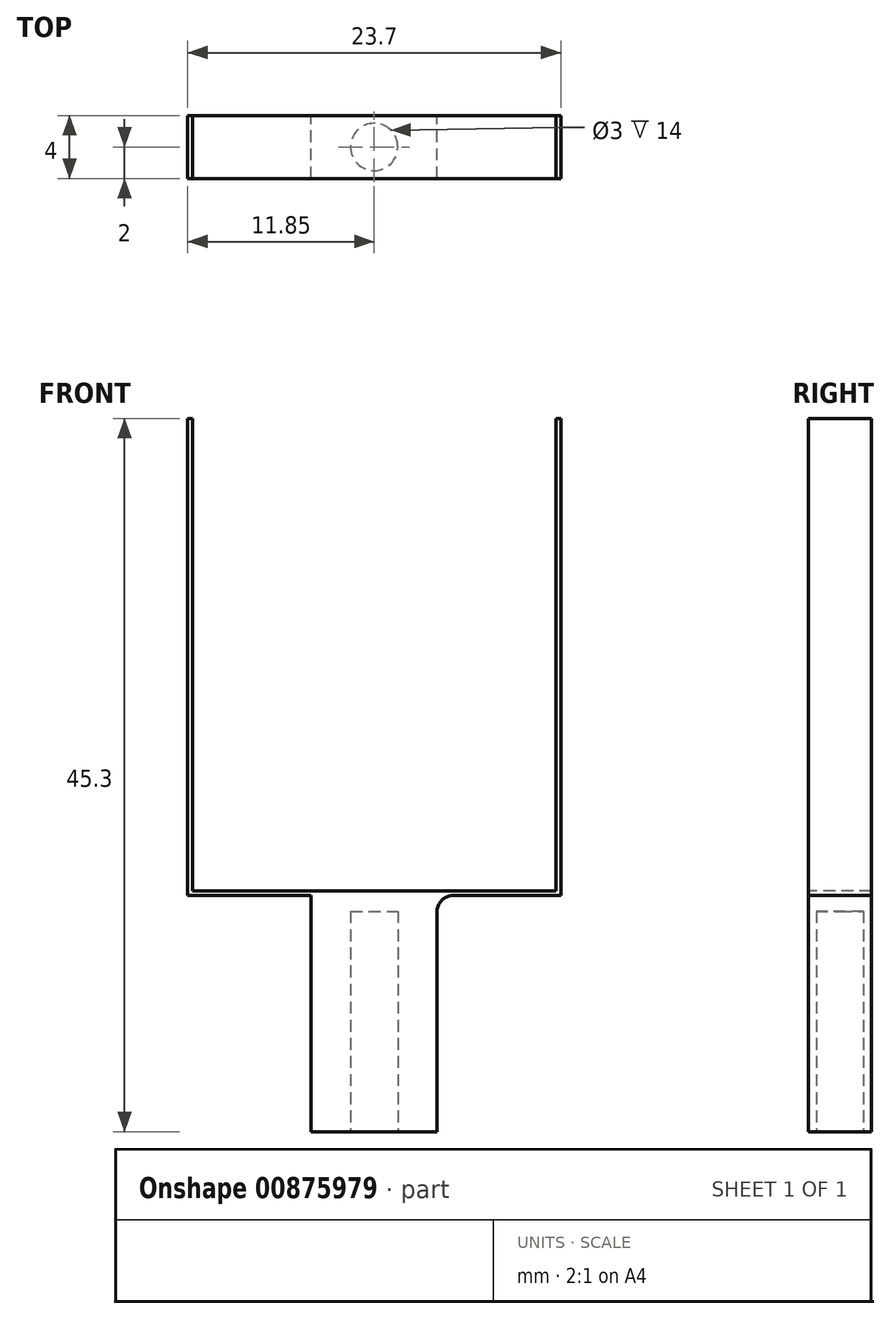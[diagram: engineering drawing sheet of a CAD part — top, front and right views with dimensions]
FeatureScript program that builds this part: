
annotation { "Feature Type Name" : "Feature", "Feature Type Description" : "" }
export const myFeature = defineFeature(function(context is Context, id is Id, definition is map)
    precondition{}
    {
        {
            var Q0;
            Q0=qCreatedBy(makeId("Top.planeOp"),FACE);
            var sketch = newSketch(context, id + "F0", { "sketchPlane" : qUnion([Q0])});
            skLineSegment(sketch, "E0.bottom", {"start": v(4, -2) * mm, "end": v(-4, -2) * mm});
            skLineSegment(sketch, "E0.top", {"start": v(4, 2) * mm, "end": v(-4, 2) * mm});
            skLineSegment(sketch, "E0.left", {"start": v(4, -2) * mm, "end": v(4, 2) * mm});
            skLineSegment(sketch, "E0.right", {"start": v(-4, -2) * mm, "end": v(-4, 2) * mm});
            skPoint(sketch, "E0.middle", {"position": v(0, 0) * mm});
            skSolve(sketch);
        }
        {
            var Q0;
            Q0=makeQuery(id+"F0.imprint","IMPRINT",FACE,{"disambiguationData":[TD([[makeQuery(id+"F0.imprint","IMPRINT",EDGE,{"derivedFrom":sQuery(id+"F0.wireOp",EDGE,"E0.bottom")}),-1.0]])]});
            extrude(context, id + "F1", {"entities" : qUnion([Q0]), "depth" : 15 * mm, "offsetDistance" : 25 * mm});
        }
        {
            var Q0;
            Q0=makeQuery(id+"F1.opExtrude","CAP_FACE",FACE,{"disambiguationData":[OSD([sQuery(id+"F0.wireOp",EDGE,"E0.bottom"),sQuery(id+"F0.wireOp",EDGE,"E0.top"),sQuery(id+"F0.wireOp",EDGE,"E0.left"),sQuery(id+"F0.wireOp",EDGE,"E0.right")])],"isStart":true});
            var sketch = newSketch(context, id + "F2", { "sketchPlane" : qUnion([Q0])});
            skCircle(sketch, "E1", {"center": v(0, 0) * mm, "radius": 1.5 * mm});
            skSolve(sketch);
        }
        {
            var Q0;
            Q0 = qSketchRegion(id + "F2", true);
            extrude(context, id + "F3", {"entities" : qUnion([Q0]), "operationType" : NewBodyOperationType.REMOVE, "oppositeDirection" : true, "depth" : 14 * mm, "offsetDistance" : 25 * mm});
        }
        {
            var Q0;
            Q0=makeQuery(id+"F1.opExtrude","CAP_FACE",FACE,{"disambiguationData":[OSD([sQuery(id+"F0.wireOp",EDGE,"E0.bottom"),sQuery(id+"F0.wireOp",EDGE,"E0.top"),sQuery(id+"F0.wireOp",EDGE,"E0.left"),sQuery(id+"F0.wireOp",EDGE,"E0.right")])],"isStart":false});
            var sketch = newSketch(context, id + "F4", { "sketchPlane" : qUnion([Q0])});
            skLineSegment(sketch, "E2.bottom", {"start": v(11.85, -2) * mm, "end": v(-11.85, -2) * mm});
            skLineSegment(sketch, "E2.top", {"start": v(11.85, 2) * mm, "end": v(-11.85, 2) * mm});
            skLineSegment(sketch, "E2.left", {"start": v(11.85, -2) * mm, "end": v(11.85, 2) * mm});
            skLineSegment(sketch, "E2.right", {"start": v(-11.85, -2) * mm, "end": v(-11.85, 2) * mm});
            skPoint(sketch, "E2.middle", {"position": v(0, 0) * mm});
            skSolve(sketch);
        }
        {
            var Q0;
            Q0 = qSketchRegion(id + "F4", true);
            extrude(context, id + "F5", {"entities" : qUnion([Q0]), "operationType" : NewBodyOperationType.ADD, "depth" : 0.3 * mm, "offsetDistance" : 25 * mm});
        }
        {
            var Q0;
            Q0=makeQuery(id+"F1.opExtrude","CAP_EDGE",EDGE,{"disambiguationData":[OSD([sQuery(id+"F0.wireOp",EDGE,"E0.right")])],"isStart":false});
            var Q1;
            Q1=makeQuery(id+"F1.opExtrude","CAP_EDGE",EDGE,{"disambiguationData":[OSD([sQuery(id+"F0.wireOp",EDGE,"E0.left")])],"isStart":false});
            fillet(context, id + "F6", {"entities" : qUnion([Q0, Q1]), "radius" : 1 * mm, "tangentPropagation" : true, "allowEdgeOverflow" : false});
        }
        {
            var Q0;
            Q0=makeQuery(id+"F5.opExtrude","CAP_FACE",FACE,{"disambiguationData":[OSD([sQuery(id+"F4.wireOp",EDGE,"E2.bottom"),sQuery(id+"F4.wireOp",EDGE,"E2.top"),sQuery(id+"F4.wireOp",EDGE,"E2.left"),sQuery(id+"F4.wireOp",EDGE,"E2.right")])],"isStart":false});
            var sketch = newSketch(context, id + "F7", { "sketchPlane" : qUnion([Q0])});
            skLineSegment(sketch, "E3.bottom", {"start": v(-11.85, 2) * mm, "end": v(-11.55, 2) * mm});
            skLineSegment(sketch, "E3.top", {"start": v(-11.85, -2) * mm, "end": v(-11.55, -2) * mm});
            skLineSegment(sketch, "E3.left", {"start": v(-11.85, 2) * mm, "end": v(-11.85, -2) * mm});
            skLineSegment(sketch, "E3.right", {"start": v(-11.55, 2) * mm, "end": v(-11.55, -2) * mm});
            skLineSegment(sketch, "E4.bottom", {"start": v(11.55, 2) * mm, "end": v(11.85, 2) * mm});
            skLineSegment(sketch, "E4.top", {"start": v(11.55, -2) * mm, "end": v(11.85, -2) * mm});
            skLineSegment(sketch, "E4.left", {"start": v(11.55, 2) * mm, "end": v(11.55, -2) * mm});
            skLineSegment(sketch, "E4.right", {"start": v(11.85, 2) * mm, "end": v(11.85, -2) * mm});
            skSolve(sketch);
        }
        {
            var Q0;
            Q0 = qSketchRegion(id + "F7", true);
            extrude(context, id + "F8", {"entities" : qUnion([Q0]), "operationType" : NewBodyOperationType.ADD, "depth" : 30 * mm, "offsetDistance" : 25 * mm});
        }
    });
